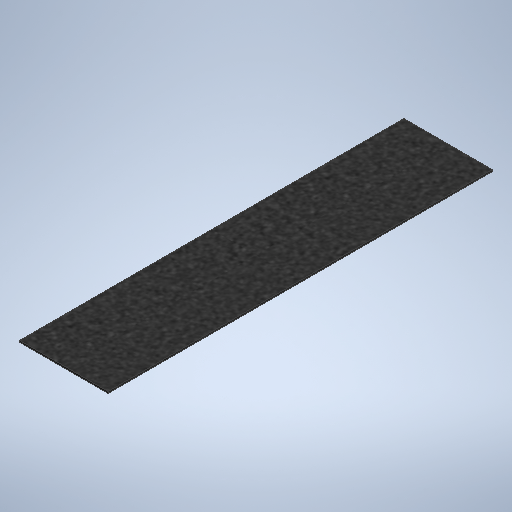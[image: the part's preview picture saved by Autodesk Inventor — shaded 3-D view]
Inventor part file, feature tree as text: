
AUTODESK INVENTOR PART (.ipt)
format: ipt  version: 2025.1 (Build 291241020, 241B)  size: 271,360 bytes
history: native  units: in
note: dims shown in document units (in); Inventor stores cm internally (conversion verified against a paired STEP export)
features: extrude x1, sketch x1
ambient origin geometry x8: Origin, YZ Plane, XZ Plane, XY Plane, X Axis, Y Axis, Z Axis, Center Point
bodies: Solid1 (feature_tree)
feature tree (2):
  extrude  "Extrusion1"  Depth=28.25in
  sketch  "Sketch1"  dims[d0=6.5in d1=28.25in d2=0.125in d3=0.0in]
